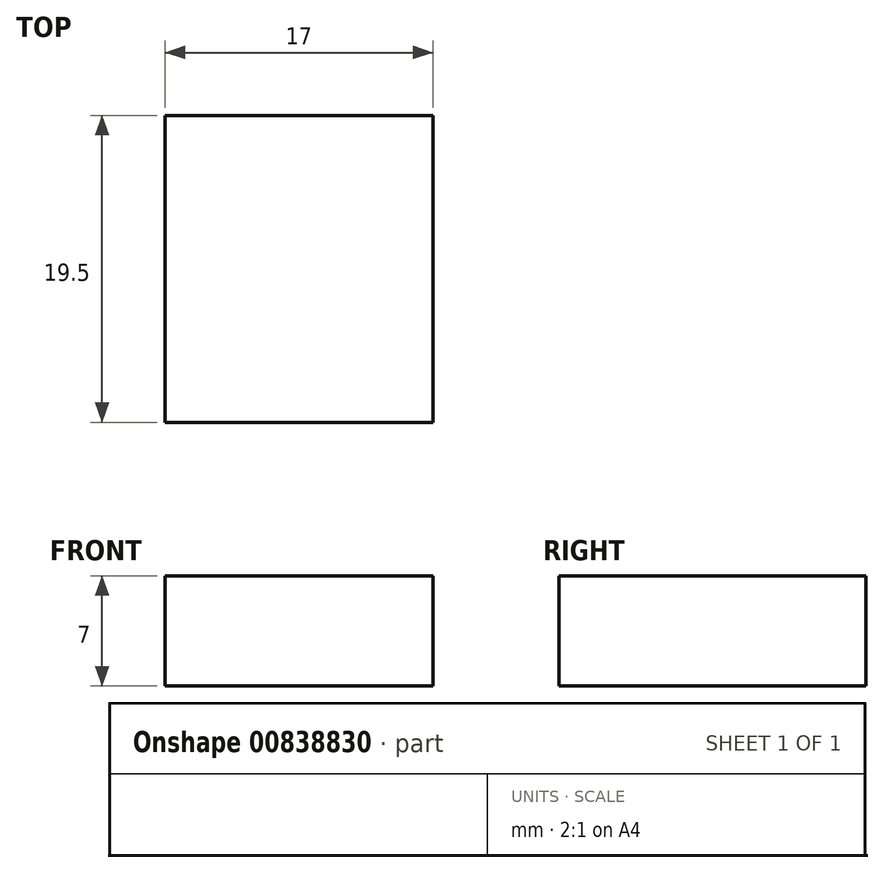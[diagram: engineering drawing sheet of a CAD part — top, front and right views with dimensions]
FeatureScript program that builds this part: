
annotation { "Feature Type Name" : "Feature", "Feature Type Description" : "" }
export const myFeature = defineFeature(function(context is Context, id is Id, definition is map)
    precondition{}
    {
        {
            var Q0;
            Q0=qCreatedBy(makeId("Top.planeOp"),FACE);
            var sketch = newSketch(context, id + "F0", { "sketchPlane" : qUnion([Q0])});
            skLineSegment(sketch, "E0.bottom", {"start": v(8.5, -9.75) * mm, "end": v(-8.5, -9.75) * mm});
            skLineSegment(sketch, "E0.top", {"start": v(8.5, 9.75) * mm, "end": v(-8.5, 9.75) * mm});
            skLineSegment(sketch, "E0.left", {"start": v(8.5, -9.75) * mm, "end": v(8.5, 9.75) * mm});
            skLineSegment(sketch, "E0.right", {"start": v(-8.5, -9.75) * mm, "end": v(-8.5, 9.75) * mm});
            skPoint(sketch, "E0.middle", {"position": v(0, 0) * mm});
            skSolve(sketch);
        }
        {
            var Q0;
            Q0 = qSketchRegion(id + "F0", true);
            extrude(context, id + "F1", {"entities" : qUnion([Q0]), "depth" : 7 * mm, "offsetDistance" : 25 * mm});
        }
    });
